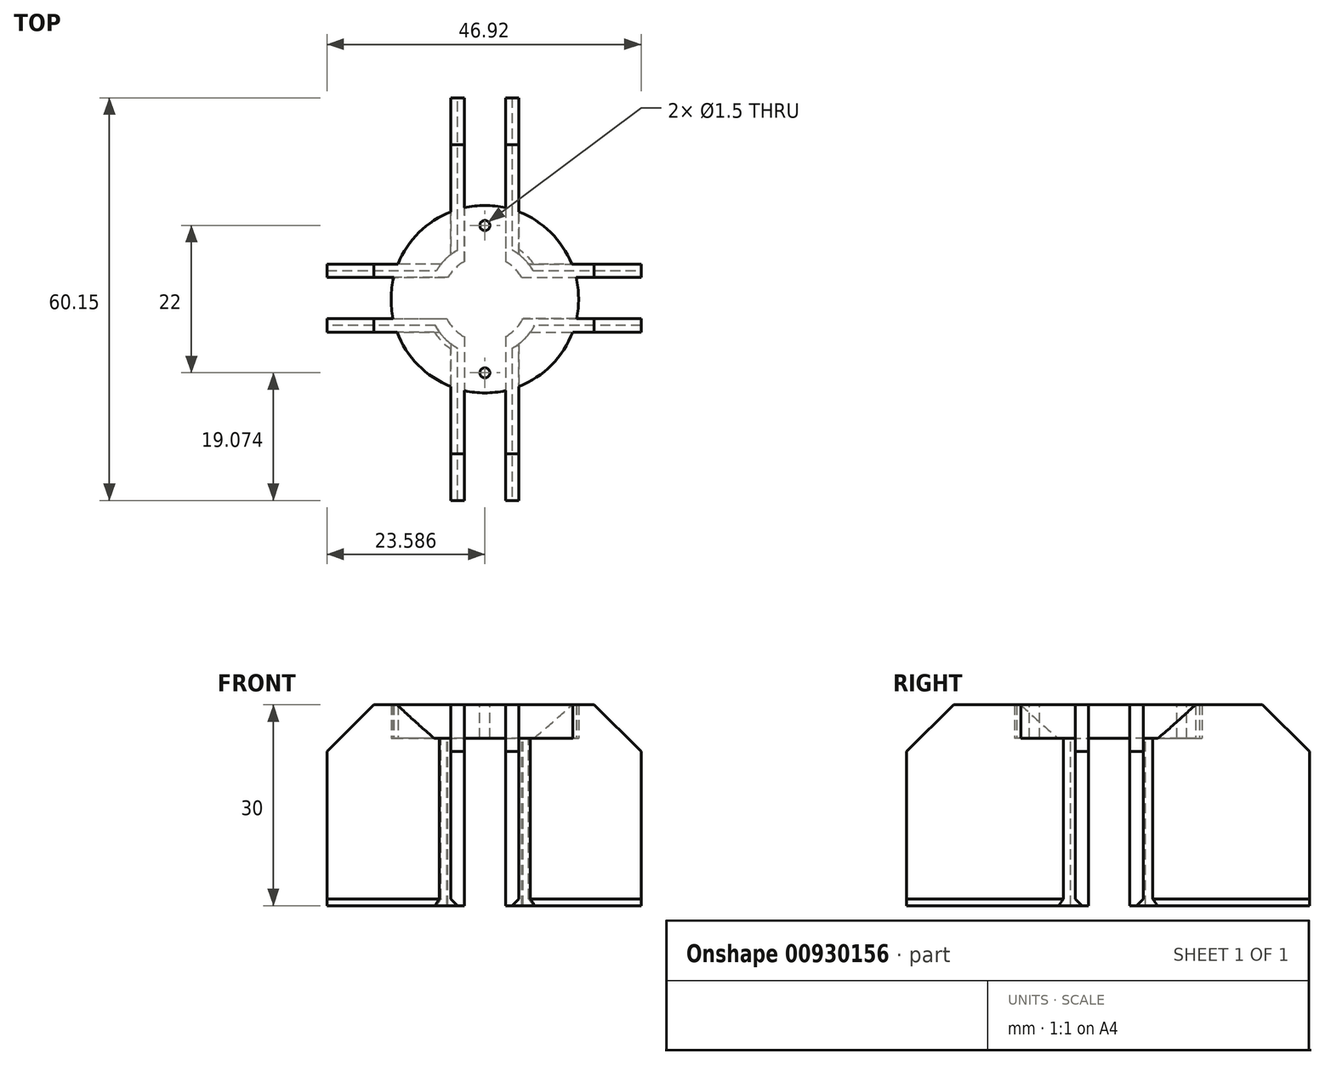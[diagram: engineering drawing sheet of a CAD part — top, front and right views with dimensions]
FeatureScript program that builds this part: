
annotation { "Feature Type Name" : "Feature", "Feature Type Description" : "" }
export const myFeature = defineFeature(function(context is Context, id is Id, definition is map)
    precondition{}
    {
        {
            var Q0;
            Q0=qCreatedBy(makeId("Top.planeOp"),FACE);
            var sketch = newSketch(context, id + "F0", { "sketchPlane" : qUnion([Q0])});
            skLineSegment(sketch, "E0.bottom", {"start": v(-2.63, 27.34) * mm, "end": v(3.52, 27.34) * mm});
            skLineSegment(sketch, "E0.top", {"start": v(-2.63, -28.81) * mm, "end": v(3.52, -28.81) * mm});
            skLineSegment(sketch, "E0.left", {"start": v(-2.63, 27.34) * mm, "end": v(-2.63, 4.86) * mm});
            skLineSegment(sketch, "E0.right", {"start": v(3.52, 27.34) * mm, "end": v(3.52, 4.86) * mm});
            skLineSegment(sketch, "E1.bottom", {"start": v(-21.14, 2.5) * mm, "end": v(-5.06, 2.5) * mm});
            skLineSegment(sketch, "E1.top", {"start": v(-21.14, -3.64) * mm, "end": v(-5.24, -3.64) * mm});
            skLineSegment(sketch, "E1.left", {"start": v(-21.14, 2.5) * mm, "end": v(-21.14, -3.64) * mm});
            skLineSegment(sketch, "E1.right", {"start": v(21.78, 2.5) * mm, "end": v(21.78, -3.64) * mm});
            skLineSegment(sketch, "E2.trimOffspring", {"start": v(-2.63, -6.34) * mm, "end": v(-2.63, -28.81) * mm});
            skLineSegment(sketch, "E3.trimOffspring", {"start": v(3.52, -6.34) * mm, "end": v(3.52, -28.81) * mm});
            skLineSegment(sketch, "E4.trimOffspring", {"start": v(5.95, 2.5) * mm, "end": v(21.78, 2.5) * mm});
            skLineSegment(sketch, "E5.trimOffspring", {"start": v(6.14, -3.64) * mm, "end": v(21.78, -3.64) * mm});
            skArc(sketch, "E6", {"start": v(-2.63, 4.86) * mm, "mid": v(-4, 3.85) * mm, "end": v(-5.06, 2.5) * mm});
            skArc(sketch, "E7.trimOffspring", {"start": v(5.95, 2.5) * mm, "mid": v(4.9, 3.85) * mm, "end": v(3.52, 4.86) * mm});
            skArc(sketch, "E8.trimOffspring", {"start": v(3.52, -6.34) * mm, "mid": v(5.03, -5.19) * mm, "end": v(6.14, -3.64) * mm});
            skArc(sketch, "E9.trimOffspring", {"start": v(-5.24, -3.64) * mm, "mid": v(-4.14, -5.19) * mm, "end": v(-2.63, -6.34) * mm});
            skLineSegment(sketch, "E10.0", {"start": v(-4.63, 29.34) * mm, "end": v(5.52, 29.34) * mm});
            skLineSegment(sketch, "E10.1", {"start": v(5.52, 29.34) * mm, "end": v(5.52, 5.94) * mm});
            skArc(sketch, "E10.2", {"start": v(7, 4.5) * mm, "mid": v(6.3, 5.27) * mm, "end": v(5.52, 5.94) * mm});
            skLineSegment(sketch, "E10.3", {"start": v(7, 4.5) * mm, "end": v(23.78, 4.5) * mm});
            skLineSegment(sketch, "E10.4", {"start": v(23.78, 4.5) * mm, "end": v(23.78, -5.64) * mm});
            skLineSegment(sketch, "E10.5", {"start": v(-23.14, -5.64) * mm, "end": v(-6.36, -5.64) * mm});
            skLineSegment(sketch, "E10.6", {"start": v(-23.14, 4.5) * mm, "end": v(-23.14, -5.64) * mm});
            skLineSegment(sketch, "E10.7", {"start": v(-23.14, 4.5) * mm, "end": v(-6.1, 4.5) * mm});
            skArc(sketch, "E10.8", {"start": v(-4.63, 5.94) * mm, "mid": v(-5.4, 5.27) * mm, "end": v(-6.1, 4.5) * mm});
            skArc(sketch, "E10.9", {"start": v(-6.36, -5.64) * mm, "mid": v(-5.56, -6.6) * mm, "end": v(-4.63, -7.42) * mm});
            skLineSegment(sketch, "E10.10", {"start": v(-4.63, -7.42) * mm, "end": v(-4.63, -30.81) * mm});
            skLineSegment(sketch, "E10.11", {"start": v(-4.63, -30.81) * mm, "end": v(5.52, -30.81) * mm});
            skLineSegment(sketch, "E10.12", {"start": v(5.52, -7.42) * mm, "end": v(5.52, -30.81) * mm});
            skArc(sketch, "E10.13", {"start": v(5.52, -7.42) * mm, "mid": v(6.45, -6.6) * mm, "end": v(7.25, -5.64) * mm});
            skLineSegment(sketch, "E10.14", {"start": v(-4.63, 29.34) * mm, "end": v(-4.63, 5.94) * mm});
            skLineSegment(sketch, "E10.15", {"start": v(7.25, -5.64) * mm, "end": v(23.78, -5.64) * mm});
            skSolve(sketch);
        }
        {
            var Q0;
            Q0=makeQuery(id+"F0.imprint","IMPRINT",FACE,{"disambiguationData":[TD([[makeQuery(id+"F0.imprint","IMPRINT",EDGE,{"derivedFrom":sQuery(id+"F0.wireOp",EDGE,"E0.bottom")}),1.0]])]});
            extrude(context, id + "F1", {"entities" : qUnion([Q0]), "oppositeDirection" : true, "depth" : 25 * mm, "offsetDistance" : 25 * mm});
        }
        {
            var Q0;
            Q0=makeQuery(id+"F1.opExtrude","CAP_FACE",FACE,{"disambiguationData":[OSD([sQuery(id+"F0.wireOp",EDGE,"E0.bottom"),sQuery(id+"F0.wireOp",EDGE,"E0.top"),sQuery(id+"F0.wireOp",EDGE,"E0.left"),sQuery(id+"F0.wireOp",EDGE,"E0.right"),sQuery(id+"F0.wireOp",EDGE,"E1.bottom"),sQuery(id+"F0.wireOp",EDGE,"E1.top"),sQuery(id+"F0.wireOp",EDGE,"E1.left"),sQuery(id+"F0.wireOp",EDGE,"E1.right"),sQuery(id+"F0.wireOp",EDGE,"E2.trimOffspring"),sQuery(id+"F0.wireOp",EDGE,"E3.trimOffspring"),sQuery(id+"F0.wireOp",EDGE,"E4.trimOffspring"),sQuery(id+"F0.wireOp",EDGE,"E5.trimOffspring"),sQuery(id+"F0.wireOp",EDGE,"E6"),sQuery(id+"F0.wireOp",EDGE,"E7.trimOffspring"),sQuery(id+"F0.wireOp",EDGE,"E8.trimOffspring"),sQuery(id+"F0.wireOp",EDGE,"E9.trimOffspring"),sQuery(id+"F0.wireOp",EDGE,"E10.0"),sQuery(id+"F0.wireOp",EDGE,"E10.1"),sQuery(id+"F0.wireOp",EDGE,"E10.2"),sQuery(id+"F0.wireOp",EDGE,"E10.3"),sQuery(id+"F0.wireOp",EDGE,"E10.4"),sQuery(id+"F0.wireOp",EDGE,"E10.5"),sQuery(id+"F0.wireOp",EDGE,"E10.6"),sQuery(id+"F0.wireOp",EDGE,"E10.7"),sQuery(id+"F0.wireOp",EDGE,"E10.8"),sQuery(id+"F0.wireOp",EDGE,"E10.9"),sQuery(id+"F0.wireOp",EDGE,"E10.10"),sQuery(id+"F0.wireOp",EDGE,"E10.11"),sQuery(id+"F0.wireOp",EDGE,"E10.12"),sQuery(id+"F0.wireOp",EDGE,"E10.13"),sQuery(id+"F0.wireOp",EDGE,"E10.14"),sQuery(id+"F0.wireOp",EDGE,"E10.15")])],"isStart":true});
            var sketch = newSketch(context, id + "F2", { "sketchPlane" : qUnion([Q0])});
            skLineSegment(sketch, "E11", {"start": v(-2.63, 27.34) * mm, "end": v(-2.63, 29.34) * mm});
            skLineSegment(sketch, "E12", {"start": v(-2.63, 29.34) * mm, "end": v(3.52, 29.34) * mm});
            skLineSegment(sketch, "E13", {"start": v(3.52, 29.34) * mm, "end": v(3.52, 27.34) * mm});
            skLineSegment(sketch, "E14", {"start": v(3.52, 27.34) * mm, "end": v(-2.63, 27.34) * mm});
            skLineSegment(sketch, "E15", {"start": v(-21.14, 2.5) * mm, "end": v(-23.14, 2.5) * mm});
            skLineSegment(sketch, "E16", {"start": v(-23.14, 2.5) * mm, "end": v(-23.14, -3.64) * mm});
            skLineSegment(sketch, "E17", {"start": v(-23.14, -3.64) * mm, "end": v(-21.14, -3.64) * mm});
            skLineSegment(sketch, "E18", {"start": v(-21.14, -3.64) * mm, "end": v(-21.14, 2.5) * mm});
            skLineSegment(sketch, "E19", {"start": v(21.78, 2.5) * mm, "end": v(23.78, 2.5) * mm});
            skLineSegment(sketch, "E20", {"start": v(23.78, 2.5) * mm, "end": v(23.78, -3.64) * mm});
            skLineSegment(sketch, "E21", {"start": v(23.78, -3.64) * mm, "end": v(21.78, -3.64) * mm});
            skLineSegment(sketch, "E22", {"start": v(21.78, -3.64) * mm, "end": v(21.78, 2.5) * mm});
            skLineSegment(sketch, "E23", {"start": v(-2.63, -28.81) * mm, "end": v(-2.63, -30.81) * mm});
            skLineSegment(sketch, "E24", {"start": v(-2.63, -30.81) * mm, "end": v(3.52, -30.81) * mm});
            skLineSegment(sketch, "E25", {"start": v(3.52, -30.81) * mm, "end": v(3.52, -28.81) * mm});
            skLineSegment(sketch, "E26", {"start": v(3.52, -28.81) * mm, "end": v(-2.63, -28.81) * mm});
            skSolve(sketch);
        }
        {
            var Q0;
            Q0=makeQuery(id+"F2.imprint","IMPRINT",FACE,{"disambiguationData":[TD([[makeQuery(id+"F2.imprint","IMPRINT",EDGE,{"derivedFrom":sQuery(id+"F2.wireOp",EDGE,"E11")}),-1.0]])]});
            var Q1;
            Q1=makeQuery(id+"F2.imprint","IMPRINT",FACE,{"disambiguationData":[TD([[makeQuery(id+"F2.imprint","IMPRINT",EDGE,{"derivedFrom":sQuery(id+"F2.wireOp",EDGE,"E15")}),1.0]])]});
            var Q2;
            Q2=makeQuery(id+"F2.imprint","IMPRINT",FACE,{"disambiguationData":[TD([[makeQuery(id+"F2.imprint","IMPRINT",EDGE,{"derivedFrom":sQuery(id+"F2.wireOp",EDGE,"E19")}),-1.0]])]});
            var Q3;
            Q3=makeQuery(id+"F2.imprint","IMPRINT",FACE,{"disambiguationData":[TD([[makeQuery(id+"F2.imprint","IMPRINT",EDGE,{"derivedFrom":sQuery(id+"F2.wireOp",EDGE,"E23")}),1.0]])]});
            extrude(context, id + "F3", {"entities" : qUnion([Q0, Q1, Q2, Q3]), "operationType" : NewBodyOperationType.REMOVE, "endBound" : BoundingType.UP_TO_NEXT, "oppositeDirection" : true, "depth" : 25 * mm, "offsetDistance" : 25 * mm});
        }
        {
            var Q0;
            Q0=qCreatedBy(makeId("Top.planeOp"),FACE);
            var sketch = newSketch(context, id + "F4", { "sketchPlane" : qUnion([Q0])});
            skLineSegment(sketch, "E27.0.0", {"start": v(5.52, 29.34) * mm, "end": v(3.52, 29.34) * mm});
            skLineSegment(sketch, "E27.0.1", {"start": v(3.52, 29.34) * mm, "end": v(3.52, 4.86) * mm});
            skArc(sketch, "E27.0.2", {"start": v(3.52, 4.86) * mm, "mid": v(4.9, 3.85) * mm, "end": v(5.95, 2.5) * mm});
            skLineSegment(sketch, "E27.0.3", {"start": v(5.95, 2.5) * mm, "end": v(23.78, 2.5) * mm});
            skLineSegment(sketch, "E27.0.4", {"start": v(23.78, 2.5) * mm, "end": v(23.78, 4.5) * mm});
            skLineSegment(sketch, "E27.0.5", {"start": v(23.78, 4.5) * mm, "end": v(7, 4.5) * mm});
            skArc(sketch, "E27.0.6", {"start": v(7, 4.5) * mm, "mid": v(6.3, 5.27) * mm, "end": v(5.52, 5.94) * mm});
            skLineSegment(sketch, "E27.0.7", {"start": v(5.52, 5.94) * mm, "end": v(5.52, 29.34) * mm});
            skArc(sketch, "E28.0.0", {"start": v(-5.06, 2.5) * mm, "mid": v(-4, 3.85) * mm, "end": v(-2.63, 4.86) * mm});
            skLineSegment(sketch, "E28.0.1", {"start": v(-2.63, 4.86) * mm, "end": v(-2.63, 29.34) * mm});
            skLineSegment(sketch, "E28.0.2", {"start": v(-2.63, 29.34) * mm, "end": v(-4.63, 29.34) * mm});
            skLineSegment(sketch, "E28.0.3", {"start": v(-4.63, 29.34) * mm, "end": v(-4.63, 5.94) * mm});
            skArc(sketch, "E28.0.4", {"start": v(-4.63, 5.94) * mm, "mid": v(-5.4, 5.27) * mm, "end": v(-6.1, 4.5) * mm});
            skLineSegment(sketch, "E28.0.5", {"start": v(-6.1, 4.5) * mm, "end": v(-23.14, 4.5) * mm});
            skLineSegment(sketch, "E28.0.6", {"start": v(-23.14, 4.5) * mm, "end": v(-23.14, 2.5) * mm});
            skLineSegment(sketch, "E28.0.7", {"start": v(-23.14, 2.5) * mm, "end": v(-5.06, 2.5) * mm});
            skLineSegment(sketch, "E29.0.0", {"start": v(-5.24, -3.64) * mm, "end": v(-23.14, -3.64) * mm});
            skLineSegment(sketch, "E29.0.1", {"start": v(-23.14, -3.64) * mm, "end": v(-23.14, -5.64) * mm});
            skLineSegment(sketch, "E29.0.2", {"start": v(-23.14, -5.64) * mm, "end": v(-6.36, -5.64) * mm});
            skArc(sketch, "E29.0.3", {"start": v(-6.36, -5.64) * mm, "mid": v(-5.56, -6.6) * mm, "end": v(-4.63, -7.42) * mm});
            skLineSegment(sketch, "E29.0.4", {"start": v(-4.63, -7.42) * mm, "end": v(-4.63, -30.81) * mm});
            skLineSegment(sketch, "E29.0.5", {"start": v(-4.63, -30.81) * mm, "end": v(-2.63, -30.81) * mm});
            skLineSegment(sketch, "E29.0.6", {"start": v(-2.63, -30.81) * mm, "end": v(-2.63, -6.34) * mm});
            skArc(sketch, "E29.0.7", {"start": v(-2.63, -6.34) * mm, "mid": v(-4.14, -5.19) * mm, "end": v(-5.24, -3.64) * mm});
            skLineSegment(sketch, "E30.0.0", {"start": v(23.78, -5.64) * mm, "end": v(23.78, -3.64) * mm});
            skLineSegment(sketch, "E30.0.1", {"start": v(23.78, -3.64) * mm, "end": v(6.14, -3.64) * mm});
            skArc(sketch, "E30.0.2", {"start": v(6.14, -3.64) * mm, "mid": v(5.03, -5.19) * mm, "end": v(3.52, -6.34) * mm});
            skLineSegment(sketch, "E30.0.3", {"start": v(3.52, -6.34) * mm, "end": v(3.52, -30.81) * mm});
            skLineSegment(sketch, "E30.0.4", {"start": v(3.52, -30.81) * mm, "end": v(5.52, -30.81) * mm});
            skLineSegment(sketch, "E30.0.5", {"start": v(5.52, -30.81) * mm, "end": v(5.52, -7.42) * mm});
            skArc(sketch, "E30.0.6", {"start": v(5.52, -7.42) * mm, "mid": v(6.45, -6.6) * mm, "end": v(7.25, -5.64) * mm});
            skLineSegment(sketch, "E30.0.7", {"start": v(7.25, -5.64) * mm, "end": v(23.78, -5.64) * mm});
            skCircle(sketch, "E31", {"center": v(0.45, -0.74) * mm, "radius": 14 * mm});
            skSolve(sketch);
        }
        {
            var Q0;
            {var subQ14=sQuery(id+"F4.wireOp",EDGE,"E27.0.2");Q0=makeQuery(id+"F4.imprint","IMPRINT",FACE,{"disambiguationData":[TD([[makeQuery(id+"F4.imprint","IMPRINT",EDGE,{"derivedFrom":subQ14}),-1.0]])]});}
            var Q1;
            {var subQ1=sQuery(id+"F4.wireOp",EDGE,"E30.0.2");Q1=makeQuery(id+"F4.imprint","IMPRINT",FACE,{"disambiguationData":[TD([[makeQuery(id+"F4.imprint","IMPRINT",EDGE,{"derivedFrom":subQ1}),1.0]])]});}
            var Q2;
            {var subQ0=sQuery(id+"F4.wireOp",EDGE,"E28.0.4");Q2=makeQuery(id+"F4.imprint","IMPRINT",FACE,{"disambiguationData":[TD([[makeQuery(id+"F4.imprint","IMPRINT",EDGE,{"derivedFrom":subQ0}),-1.0]])]});}
            var Q3;
            {var subQ2=sQuery(id+"F4.wireOp",EDGE,"E28.0.0");Q3=makeQuery(id+"F4.imprint","IMPRINT",FACE,{"disambiguationData":[TD([[makeQuery(id+"F4.imprint","IMPRINT",EDGE,{"derivedFrom":subQ2}),1.0]])]});}
            var Q4;
            {var subQ0=sQuery(id+"F4.wireOp",EDGE,"E27.0.6");Q4=makeQuery(id+"F4.imprint","IMPRINT",FACE,{"disambiguationData":[TD([[makeQuery(id+"F4.imprint","IMPRINT",EDGE,{"derivedFrom":subQ0}),-1.0]])]});}
            var Q5;
            {var subQ1=sQuery(id+"F4.wireOp",EDGE,"E27.0.2");Q5=makeQuery(id+"F4.imprint","IMPRINT",FACE,{"disambiguationData":[TD([[makeQuery(id+"F4.imprint","IMPRINT",EDGE,{"derivedFrom":subQ1}),1.0]])]});}
            var Q6;
            {var subQ0=sQuery(id+"F4.wireOp",EDGE,"E30.0.6");Q6=makeQuery(id+"F4.imprint","IMPRINT",FACE,{"disambiguationData":[TD([[makeQuery(id+"F4.imprint","IMPRINT",EDGE,{"derivedFrom":subQ0}),-1.0]])]});}
            var Q7;
            {var subQ0=sQuery(id+"F4.wireOp",EDGE,"E29.0.3");Q7=makeQuery(id+"F4.imprint","IMPRINT",FACE,{"disambiguationData":[TD([[makeQuery(id+"F4.imprint","IMPRINT",EDGE,{"derivedFrom":subQ0}),-1.0]])]});}
            var Q8;
            {var subQ1=sQuery(id+"F4.wireOp",EDGE,"E29.0.3");Q8=makeQuery(id+"F4.imprint","IMPRINT",FACE,{"disambiguationData":[TD([[makeQuery(id+"F4.imprint","IMPRINT",EDGE,{"derivedFrom":subQ1}),1.0]])]});}
            extrude(context, id + "F5", {"entities" : qUnion([Q0, Q1, Q2, Q3, Q4, Q5, Q6, Q7, Q8]), "operationType" : NewBodyOperationType.ADD, "depth" : 5 * mm, "offsetDistance" : 25 * mm});
        }
        {
            var Q0;
            Q0=makeQuery(id+"F5.opExtrude","CAP_FACE",FACE,{"disambiguationData":[OSD([sQuery(id+"F4.wireOp",EDGE,"E31")])],"isStart":false});
            var sketch = newSketch(context, id + "F6", { "sketchPlane" : qUnion([Q0])});
            skCircle(sketch, "E32", {"center": v(0.45, 10.26) * mm, "radius": 0.75 * mm});
            skCircle(sketch, "E33", {"center": v(0.45, -11.74) * mm, "radius": 0.75 * mm});
            skLineSegment(sketch, "E34", {"start": v(0.45, 10.26) * mm, "end": v(0.45, -11.74) * mm, "construction": true});
            skLineSegment(sketch, "E35", {"start": v(0.45, 10.26) * mm, "end": v(0.45, 13.26) * mm, "construction": true});
            skPoint(sketch, "E36.startSnap0", {"position": v(0.45, -0.74) * mm});
            skLineSegment(sketch, "E37.0", {"start": v(-2.63, 12.92) * mm, "end": v(-2.63, 29.34) * mm, "construction": true});
            skLineSegment(sketch, "E38.0", {"start": v(3.52, 29.34) * mm, "end": v(3.52, 12.92) * mm, "construction": true});
            skLineSegment(sketch, "E39", {"start": v(-2.63, 21.13) * mm, "end": v(0.45, 13.26) * mm, "construction": true});
            skLineSegment(sketch, "E40", {"start": v(3.52, 21.13) * mm, "end": v(0.45, 13.26) * mm, "construction": true});
            skLineSegment(sketch, "E41.0", {"start": v(3.52, -14.4) * mm, "end": v(3.52, -30.81) * mm, "construction": true});
            skLineSegment(sketch, "E42.0", {"start": v(-2.63, -14.4) * mm, "end": v(-2.63, -30.81) * mm, "construction": true});
            skLineSegment(sketch, "E43", {"start": v(-2.63, -22.6) * mm, "end": v(0.45, -14.74) * mm, "construction": true});
            skLineSegment(sketch, "E44", {"start": v(3.52, -22.6) * mm, "end": v(0.45, -14.74) * mm, "construction": true});
            skLineSegment(sketch, "E45", {"start": v(0.45, -11.74) * mm, "end": v(0.45, -14.74) * mm, "construction": true});
            skSolve(sketch);
        }
        {
            var Q0;
            Q0=makeQuery(id+"F6.imprint","IMPRINT",FACE,{"disambiguationData":[TD([[makeQuery(id+"F6.imprint","IMPRINT",EDGE,{"derivedFrom":sQuery(id+"F6.wireOp",EDGE,"E32")}),1.0]])]});
            var Q1;
            Q1=makeQuery(id+"F6.imprint","IMPRINT",FACE,{"disambiguationData":[TD([[makeQuery(id+"F6.imprint","IMPRINT",EDGE,{"derivedFrom":sQuery(id+"F6.wireOp",EDGE,"E33")}),1.0]])]});
            extrude(context, id + "F7", {"entities" : qUnion([Q0, Q1]), "operationType" : NewBodyOperationType.REMOVE, "endBound" : BoundingType.UP_TO_NEXT, "oppositeDirection" : true, "depth" : 25 * mm, "offsetDistance" : 25 * mm});
        }
        {
            var Q0;
            {var subQ1=sQuery(id+"F0.wireOp",EDGE,"E10.14");var subQ3=sQuery(id+"F0.wireOp",EDGE,"E10.0");var subQ5=sQuery(id+"F0.wireOp",EDGE,"E0.left");var subQ6=makeQuery(id+"F1.opExtrude","SWEPT_FACE",FACE,{"disambiguationData":[OSD([subQ5])]});var subQ7=sQuery(id+"F0.wireOp",EDGE,"E1.bottom");var subQ8=sQuery(id+"F0.wireOp",EDGE,"E6");var subQ9=sQuery(id+"F0.wireOp",EDGE,"E10.7");var subQ10=sQuery(id+"F0.wireOp",EDGE,"E10.8");var subQ11=sQuery(id+"F0.wireOp",EDGE,"E10.6");Q0=makeQuery(id+"F5.boolean.opBoolean","SPLIT",FACE,{"disambiguationData":[TD([subQ6])],"derivedFrom":makeQuery(id+"F3.boolean.opBoolean","SPLIT",FACE,{"disambiguationData":[TD([subQ6])],"derivedFrom":makeQuery(id+"F1.opExtrude","CAP_FACE",FACE,{"disambiguationData":[OSD([sQuery(id+"F0.wireOp",EDGE,"E0.bottom"),sQuery(id+"F0.wireOp",EDGE,"E0.top"),subQ5,sQuery(id+"F0.wireOp",EDGE,"E0.right"),subQ7,sQuery(id+"F0.wireOp",EDGE,"E1.top"),sQuery(id+"F0.wireOp",EDGE,"E1.left"),sQuery(id+"F0.wireOp",EDGE,"E1.right"),sQuery(id+"F0.wireOp",EDGE,"E2.trimOffspring"),sQuery(id+"F0.wireOp",EDGE,"E3.trimOffspring"),sQuery(id+"F0.wireOp",EDGE,"E4.trimOffspring"),sQuery(id+"F0.wireOp",EDGE,"E5.trimOffspring"),subQ8,sQuery(id+"F0.wireOp",EDGE,"E7.trimOffspring"),sQuery(id+"F0.wireOp",EDGE,"E8.trimOffspring"),sQuery(id+"F0.wireOp",EDGE,"E9.trimOffspring"),subQ3,sQuery(id+"F0.wireOp",EDGE,"E10.1"),sQuery(id+"F0.wireOp",EDGE,"E10.2"),sQuery(id+"F0.wireOp",EDGE,"E10.3"),sQuery(id+"F0.wireOp",EDGE,"E10.4"),sQuery(id+"F0.wireOp",EDGE,"E10.5"),subQ11,subQ9,subQ10,sQuery(id+"F0.wireOp",EDGE,"E10.9"),sQuery(id+"F0.wireOp",EDGE,"E10.10"),sQuery(id+"F0.wireOp",EDGE,"E10.11"),sQuery(id+"F0.wireOp",EDGE,"E10.12"),sQuery(id+"F0.wireOp",EDGE,"E10.13"),subQ1,sQuery(id+"F0.wireOp",EDGE,"E10.15")])],"isStart":true})})});}
            var Q1;
            {var subQ1=sQuery(id+"F0.wireOp",EDGE,"E10.1");var subQ3=sQuery(id+"F0.wireOp",EDGE,"E10.0");var subQ5=sQuery(id+"F0.wireOp",EDGE,"E0.right");var subQ6=makeQuery(id+"F1.opExtrude","SWEPT_FACE",FACE,{"disambiguationData":[OSD([subQ5])]});var subQ7=sQuery(id+"F0.wireOp",EDGE,"E4.trimOffspring");var subQ8=sQuery(id+"F0.wireOp",EDGE,"E7.trimOffspring");var subQ9=sQuery(id+"F0.wireOp",EDGE,"E10.2");var subQ10=sQuery(id+"F0.wireOp",EDGE,"E10.3");var subQ11=sQuery(id+"F0.wireOp",EDGE,"E10.4");Q1=makeQuery(id+"F5.boolean.opBoolean","SPLIT",FACE,{"disambiguationData":[TD([subQ6])],"derivedFrom":makeQuery(id+"F3.boolean.opBoolean","SPLIT",FACE,{"disambiguationData":[TD([subQ6])],"derivedFrom":makeQuery(id+"F1.opExtrude","CAP_FACE",FACE,{"disambiguationData":[OSD([sQuery(id+"F0.wireOp",EDGE,"E0.bottom"),sQuery(id+"F0.wireOp",EDGE,"E0.top"),sQuery(id+"F0.wireOp",EDGE,"E0.left"),subQ5,sQuery(id+"F0.wireOp",EDGE,"E1.bottom"),sQuery(id+"F0.wireOp",EDGE,"E1.top"),sQuery(id+"F0.wireOp",EDGE,"E1.left"),sQuery(id+"F0.wireOp",EDGE,"E1.right"),sQuery(id+"F0.wireOp",EDGE,"E2.trimOffspring"),sQuery(id+"F0.wireOp",EDGE,"E3.trimOffspring"),subQ7,sQuery(id+"F0.wireOp",EDGE,"E5.trimOffspring"),sQuery(id+"F0.wireOp",EDGE,"E6"),subQ8,sQuery(id+"F0.wireOp",EDGE,"E8.trimOffspring"),sQuery(id+"F0.wireOp",EDGE,"E9.trimOffspring"),subQ3,subQ1,subQ9,subQ10,subQ11,sQuery(id+"F0.wireOp",EDGE,"E10.5"),sQuery(id+"F0.wireOp",EDGE,"E10.6"),sQuery(id+"F0.wireOp",EDGE,"E10.7"),sQuery(id+"F0.wireOp",EDGE,"E10.8"),sQuery(id+"F0.wireOp",EDGE,"E10.9"),sQuery(id+"F0.wireOp",EDGE,"E10.10"),sQuery(id+"F0.wireOp",EDGE,"E10.11"),sQuery(id+"F0.wireOp",EDGE,"E10.12"),sQuery(id+"F0.wireOp",EDGE,"E10.13"),sQuery(id+"F0.wireOp",EDGE,"E10.14"),sQuery(id+"F0.wireOp",EDGE,"E10.15")])],"isStart":true})})});}
            var Q2;
            {var subQ0=sQuery(id+"F0.wireOp",EDGE,"E10.3");var subQ3=sQuery(id+"F0.wireOp",EDGE,"E10.4");var subQ5=sQuery(id+"F0.wireOp",EDGE,"E4.trimOffspring");var subQ6=makeQuery(id+"F1.opExtrude","SWEPT_FACE",FACE,{"disambiguationData":[OSD([subQ5])]});var subQ7=sQuery(id+"F0.wireOp",EDGE,"E10.0");var subQ8=sQuery(id+"F0.wireOp",EDGE,"E7.trimOffspring");var subQ9=sQuery(id+"F0.wireOp",EDGE,"E0.right");var subQ10=sQuery(id+"F0.wireOp",EDGE,"E10.1");var subQ11=sQuery(id+"F0.wireOp",EDGE,"E10.2");Q2=makeQuery(id+"F5.boolean.opBoolean","SPLIT",FACE,{"disambiguationData":[TD([subQ6])],"derivedFrom":makeQuery(id+"F3.boolean.opBoolean","SPLIT",FACE,{"disambiguationData":[TD([makeQuery(id+"F1.opExtrude","SWEPT_FACE",FACE,{"disambiguationData":[OSD([subQ9])]})])],"derivedFrom":makeQuery(id+"F1.opExtrude","CAP_FACE",FACE,{"disambiguationData":[OSD([sQuery(id+"F0.wireOp",EDGE,"E0.bottom"),sQuery(id+"F0.wireOp",EDGE,"E0.top"),sQuery(id+"F0.wireOp",EDGE,"E0.left"),subQ9,sQuery(id+"F0.wireOp",EDGE,"E1.bottom"),sQuery(id+"F0.wireOp",EDGE,"E1.top"),sQuery(id+"F0.wireOp",EDGE,"E1.left"),sQuery(id+"F0.wireOp",EDGE,"E1.right"),sQuery(id+"F0.wireOp",EDGE,"E2.trimOffspring"),sQuery(id+"F0.wireOp",EDGE,"E3.trimOffspring"),subQ5,sQuery(id+"F0.wireOp",EDGE,"E5.trimOffspring"),sQuery(id+"F0.wireOp",EDGE,"E6"),subQ8,sQuery(id+"F0.wireOp",EDGE,"E8.trimOffspring"),sQuery(id+"F0.wireOp",EDGE,"E9.trimOffspring"),subQ7,subQ10,subQ11,subQ0,subQ3,sQuery(id+"F0.wireOp",EDGE,"E10.5"),sQuery(id+"F0.wireOp",EDGE,"E10.6"),sQuery(id+"F0.wireOp",EDGE,"E10.7"),sQuery(id+"F0.wireOp",EDGE,"E10.8"),sQuery(id+"F0.wireOp",EDGE,"E10.9"),sQuery(id+"F0.wireOp",EDGE,"E10.10"),sQuery(id+"F0.wireOp",EDGE,"E10.11"),sQuery(id+"F0.wireOp",EDGE,"E10.12"),sQuery(id+"F0.wireOp",EDGE,"E10.13"),sQuery(id+"F0.wireOp",EDGE,"E10.14"),sQuery(id+"F0.wireOp",EDGE,"E10.15")])],"isStart":true})})});}
            var Q3;
            {var subQ1=sQuery(id+"F0.wireOp",EDGE,"E10.4");var subQ3=sQuery(id+"F0.wireOp",EDGE,"E10.15");var subQ5=sQuery(id+"F0.wireOp",EDGE,"E5.trimOffspring");var subQ6=makeQuery(id+"F1.opExtrude","SWEPT_FACE",FACE,{"disambiguationData":[OSD([subQ5])]});var subQ7=sQuery(id+"F0.wireOp",EDGE,"E3.trimOffspring");var subQ8=sQuery(id+"F0.wireOp",EDGE,"E8.trimOffspring");var subQ9=sQuery(id+"F0.wireOp",EDGE,"E10.11");var subQ10=sQuery(id+"F0.wireOp",EDGE,"E10.12");var subQ11=sQuery(id+"F0.wireOp",EDGE,"E10.13");Q3=makeQuery(id+"F5.boolean.opBoolean","SPLIT",FACE,{"disambiguationData":[TD([subQ6])],"derivedFrom":makeQuery(id+"F3.boolean.opBoolean","SPLIT",FACE,{"disambiguationData":[TD([makeQuery(id+"F1.opExtrude","SWEPT_FACE",FACE,{"disambiguationData":[OSD([subQ7])]})])],"derivedFrom":makeQuery(id+"F1.opExtrude","CAP_FACE",FACE,{"disambiguationData":[OSD([sQuery(id+"F0.wireOp",EDGE,"E0.bottom"),sQuery(id+"F0.wireOp",EDGE,"E0.top"),sQuery(id+"F0.wireOp",EDGE,"E0.left"),sQuery(id+"F0.wireOp",EDGE,"E0.right"),sQuery(id+"F0.wireOp",EDGE,"E1.bottom"),sQuery(id+"F0.wireOp",EDGE,"E1.top"),sQuery(id+"F0.wireOp",EDGE,"E1.left"),sQuery(id+"F0.wireOp",EDGE,"E1.right"),sQuery(id+"F0.wireOp",EDGE,"E2.trimOffspring"),subQ7,sQuery(id+"F0.wireOp",EDGE,"E4.trimOffspring"),subQ5,sQuery(id+"F0.wireOp",EDGE,"E6"),sQuery(id+"F0.wireOp",EDGE,"E7.trimOffspring"),subQ8,sQuery(id+"F0.wireOp",EDGE,"E9.trimOffspring"),sQuery(id+"F0.wireOp",EDGE,"E10.0"),sQuery(id+"F0.wireOp",EDGE,"E10.1"),sQuery(id+"F0.wireOp",EDGE,"E10.2"),sQuery(id+"F0.wireOp",EDGE,"E10.3"),subQ1,sQuery(id+"F0.wireOp",EDGE,"E10.5"),sQuery(id+"F0.wireOp",EDGE,"E10.6"),sQuery(id+"F0.wireOp",EDGE,"E10.7"),sQuery(id+"F0.wireOp",EDGE,"E10.8"),sQuery(id+"F0.wireOp",EDGE,"E10.9"),sQuery(id+"F0.wireOp",EDGE,"E10.10"),subQ9,subQ10,subQ11,sQuery(id+"F0.wireOp",EDGE,"E10.14"),subQ3])],"isStart":true})})});}
            var Q4;
            {var subQ1=sQuery(id+"F0.wireOp",EDGE,"E1.bottom");var subQ2=makeQuery(id+"F1.opExtrude","SWEPT_FACE",FACE,{"disambiguationData":[OSD([subQ1])]});var subQ3=sQuery(id+"F0.wireOp",EDGE,"E10.7");var subQ5=sQuery(id+"F0.wireOp",EDGE,"E10.6");var subQ7=sQuery(id+"F0.wireOp",EDGE,"E10.0");var subQ8=sQuery(id+"F0.wireOp",EDGE,"E6");var subQ9=sQuery(id+"F0.wireOp",EDGE,"E0.left");var subQ10=sQuery(id+"F0.wireOp",EDGE,"E10.8");var subQ11=sQuery(id+"F0.wireOp",EDGE,"E10.14");Q4=makeQuery(id+"F5.boolean.opBoolean","SPLIT",FACE,{"disambiguationData":[TD([subQ2])],"derivedFrom":makeQuery(id+"F3.boolean.opBoolean","SPLIT",FACE,{"disambiguationData":[TD([makeQuery(id+"F1.opExtrude","SWEPT_FACE",FACE,{"disambiguationData":[OSD([subQ9])]})])],"derivedFrom":makeQuery(id+"F1.opExtrude","CAP_FACE",FACE,{"disambiguationData":[OSD([sQuery(id+"F0.wireOp",EDGE,"E0.bottom"),sQuery(id+"F0.wireOp",EDGE,"E0.top"),subQ9,sQuery(id+"F0.wireOp",EDGE,"E0.right"),subQ1,sQuery(id+"F0.wireOp",EDGE,"E1.top"),sQuery(id+"F0.wireOp",EDGE,"E1.left"),sQuery(id+"F0.wireOp",EDGE,"E1.right"),sQuery(id+"F0.wireOp",EDGE,"E2.trimOffspring"),sQuery(id+"F0.wireOp",EDGE,"E3.trimOffspring"),sQuery(id+"F0.wireOp",EDGE,"E4.trimOffspring"),sQuery(id+"F0.wireOp",EDGE,"E5.trimOffspring"),subQ8,sQuery(id+"F0.wireOp",EDGE,"E7.trimOffspring"),sQuery(id+"F0.wireOp",EDGE,"E8.trimOffspring"),sQuery(id+"F0.wireOp",EDGE,"E9.trimOffspring"),subQ7,sQuery(id+"F0.wireOp",EDGE,"E10.1"),sQuery(id+"F0.wireOp",EDGE,"E10.2"),sQuery(id+"F0.wireOp",EDGE,"E10.3"),sQuery(id+"F0.wireOp",EDGE,"E10.4"),sQuery(id+"F0.wireOp",EDGE,"E10.5"),subQ5,subQ3,subQ10,sQuery(id+"F0.wireOp",EDGE,"E10.9"),sQuery(id+"F0.wireOp",EDGE,"E10.10"),sQuery(id+"F0.wireOp",EDGE,"E10.11"),sQuery(id+"F0.wireOp",EDGE,"E10.12"),sQuery(id+"F0.wireOp",EDGE,"E10.13"),subQ11,sQuery(id+"F0.wireOp",EDGE,"E10.15")])],"isStart":true})})});}
            var Q5;
            {var subQ0=sQuery(id+"F0.wireOp",EDGE,"E10.6");var subQ2=sQuery(id+"F0.wireOp",EDGE,"E10.5");var subQ5=sQuery(id+"F0.wireOp",EDGE,"E1.top");var subQ6=makeQuery(id+"F1.opExtrude","SWEPT_FACE",FACE,{"disambiguationData":[OSD([subQ5])]});var subQ7=sQuery(id+"F0.wireOp",EDGE,"E2.trimOffspring");var subQ8=sQuery(id+"F0.wireOp",EDGE,"E9.trimOffspring");var subQ9=sQuery(id+"F0.wireOp",EDGE,"E10.10");var subQ10=sQuery(id+"F0.wireOp",EDGE,"E10.11");var subQ11=sQuery(id+"F0.wireOp",EDGE,"E10.9");Q5=makeQuery(id+"F5.boolean.opBoolean","SPLIT",FACE,{"disambiguationData":[TD([subQ6])],"derivedFrom":makeQuery(id+"F3.boolean.opBoolean","SPLIT",FACE,{"disambiguationData":[TD([subQ6])],"derivedFrom":makeQuery(id+"F1.opExtrude","CAP_FACE",FACE,{"disambiguationData":[OSD([sQuery(id+"F0.wireOp",EDGE,"E0.bottom"),sQuery(id+"F0.wireOp",EDGE,"E0.top"),sQuery(id+"F0.wireOp",EDGE,"E0.left"),sQuery(id+"F0.wireOp",EDGE,"E0.right"),sQuery(id+"F0.wireOp",EDGE,"E1.bottom"),subQ5,sQuery(id+"F0.wireOp",EDGE,"E1.left"),sQuery(id+"F0.wireOp",EDGE,"E1.right"),subQ7,sQuery(id+"F0.wireOp",EDGE,"E3.trimOffspring"),sQuery(id+"F0.wireOp",EDGE,"E4.trimOffspring"),sQuery(id+"F0.wireOp",EDGE,"E5.trimOffspring"),sQuery(id+"F0.wireOp",EDGE,"E6"),sQuery(id+"F0.wireOp",EDGE,"E7.trimOffspring"),sQuery(id+"F0.wireOp",EDGE,"E8.trimOffspring"),subQ8,sQuery(id+"F0.wireOp",EDGE,"E10.0"),sQuery(id+"F0.wireOp",EDGE,"E10.1"),sQuery(id+"F0.wireOp",EDGE,"E10.2"),sQuery(id+"F0.wireOp",EDGE,"E10.3"),sQuery(id+"F0.wireOp",EDGE,"E10.4"),subQ2,subQ0,sQuery(id+"F0.wireOp",EDGE,"E10.7"),sQuery(id+"F0.wireOp",EDGE,"E10.8"),subQ11,subQ9,subQ10,sQuery(id+"F0.wireOp",EDGE,"E10.12"),sQuery(id+"F0.wireOp",EDGE,"E10.13"),sQuery(id+"F0.wireOp",EDGE,"E10.14"),sQuery(id+"F0.wireOp",EDGE,"E10.15")])],"isStart":true})})});}
            var Q6;
            {var subQ1=sQuery(id+"F0.wireOp",EDGE,"E10.10");var subQ3=sQuery(id+"F0.wireOp",EDGE,"E10.11");var subQ5=sQuery(id+"F0.wireOp",EDGE,"E2.trimOffspring");var subQ6=makeQuery(id+"F1.opExtrude","SWEPT_FACE",FACE,{"disambiguationData":[OSD([subQ5])]});var subQ7=sQuery(id+"F0.wireOp",EDGE,"E10.5");var subQ8=sQuery(id+"F0.wireOp",EDGE,"E9.trimOffspring");var subQ9=sQuery(id+"F0.wireOp",EDGE,"E1.top");var subQ10=sQuery(id+"F0.wireOp",EDGE,"E10.6");var subQ11=sQuery(id+"F0.wireOp",EDGE,"E10.9");Q6=makeQuery(id+"F5.boolean.opBoolean","SPLIT",FACE,{"disambiguationData":[TD([subQ6])],"derivedFrom":makeQuery(id+"F3.boolean.opBoolean","SPLIT",FACE,{"disambiguationData":[TD([makeQuery(id+"F1.opExtrude","SWEPT_FACE",FACE,{"disambiguationData":[OSD([subQ9])]})])],"derivedFrom":makeQuery(id+"F1.opExtrude","CAP_FACE",FACE,{"disambiguationData":[OSD([sQuery(id+"F0.wireOp",EDGE,"E0.bottom"),sQuery(id+"F0.wireOp",EDGE,"E0.top"),sQuery(id+"F0.wireOp",EDGE,"E0.left"),sQuery(id+"F0.wireOp",EDGE,"E0.right"),sQuery(id+"F0.wireOp",EDGE,"E1.bottom"),subQ9,sQuery(id+"F0.wireOp",EDGE,"E1.left"),sQuery(id+"F0.wireOp",EDGE,"E1.right"),subQ5,sQuery(id+"F0.wireOp",EDGE,"E3.trimOffspring"),sQuery(id+"F0.wireOp",EDGE,"E4.trimOffspring"),sQuery(id+"F0.wireOp",EDGE,"E5.trimOffspring"),sQuery(id+"F0.wireOp",EDGE,"E6"),sQuery(id+"F0.wireOp",EDGE,"E7.trimOffspring"),sQuery(id+"F0.wireOp",EDGE,"E8.trimOffspring"),subQ8,sQuery(id+"F0.wireOp",EDGE,"E10.0"),sQuery(id+"F0.wireOp",EDGE,"E10.1"),sQuery(id+"F0.wireOp",EDGE,"E10.2"),sQuery(id+"F0.wireOp",EDGE,"E10.3"),sQuery(id+"F0.wireOp",EDGE,"E10.4"),subQ7,subQ10,sQuery(id+"F0.wireOp",EDGE,"E10.7"),sQuery(id+"F0.wireOp",EDGE,"E10.8"),subQ11,subQ1,subQ3,sQuery(id+"F0.wireOp",EDGE,"E10.12"),sQuery(id+"F0.wireOp",EDGE,"E10.13"),sQuery(id+"F0.wireOp",EDGE,"E10.14"),sQuery(id+"F0.wireOp",EDGE,"E10.15")])],"isStart":true})})});}
            var Q7;
            {var subQ1=sQuery(id+"F0.wireOp",EDGE,"E10.12");var subQ3=sQuery(id+"F0.wireOp",EDGE,"E10.11");var subQ5=sQuery(id+"F0.wireOp",EDGE,"E3.trimOffspring");var subQ6=makeQuery(id+"F1.opExtrude","SWEPT_FACE",FACE,{"disambiguationData":[OSD([subQ5])]});var subQ7=sQuery(id+"F0.wireOp",EDGE,"E10.4");var subQ8=sQuery(id+"F0.wireOp",EDGE,"E10.15");var subQ9=sQuery(id+"F0.wireOp",EDGE,"E5.trimOffspring");var subQ10=sQuery(id+"F0.wireOp",EDGE,"E8.trimOffspring");var subQ11=sQuery(id+"F0.wireOp",EDGE,"E10.13");Q7=makeQuery(id+"F5.boolean.opBoolean","SPLIT",FACE,{"disambiguationData":[TD([subQ6])],"derivedFrom":makeQuery(id+"F3.boolean.opBoolean","SPLIT",FACE,{"disambiguationData":[TD([subQ6])],"derivedFrom":makeQuery(id+"F1.opExtrude","CAP_FACE",FACE,{"disambiguationData":[OSD([sQuery(id+"F0.wireOp",EDGE,"E0.bottom"),sQuery(id+"F0.wireOp",EDGE,"E0.top"),sQuery(id+"F0.wireOp",EDGE,"E0.left"),sQuery(id+"F0.wireOp",EDGE,"E0.right"),sQuery(id+"F0.wireOp",EDGE,"E1.bottom"),sQuery(id+"F0.wireOp",EDGE,"E1.top"),sQuery(id+"F0.wireOp",EDGE,"E1.left"),sQuery(id+"F0.wireOp",EDGE,"E1.right"),sQuery(id+"F0.wireOp",EDGE,"E2.trimOffspring"),subQ5,sQuery(id+"F0.wireOp",EDGE,"E4.trimOffspring"),subQ9,sQuery(id+"F0.wireOp",EDGE,"E6"),sQuery(id+"F0.wireOp",EDGE,"E7.trimOffspring"),subQ10,sQuery(id+"F0.wireOp",EDGE,"E9.trimOffspring"),sQuery(id+"F0.wireOp",EDGE,"E10.0"),sQuery(id+"F0.wireOp",EDGE,"E10.1"),sQuery(id+"F0.wireOp",EDGE,"E10.2"),sQuery(id+"F0.wireOp",EDGE,"E10.3"),subQ7,sQuery(id+"F0.wireOp",EDGE,"E10.5"),sQuery(id+"F0.wireOp",EDGE,"E10.6"),sQuery(id+"F0.wireOp",EDGE,"E10.7"),sQuery(id+"F0.wireOp",EDGE,"E10.8"),sQuery(id+"F0.wireOp",EDGE,"E10.9"),sQuery(id+"F0.wireOp",EDGE,"E10.10"),subQ3,subQ1,subQ11,sQuery(id+"F0.wireOp",EDGE,"E10.14"),subQ8])],"isStart":true})})});}
            extrude(context, id + "F8", {"entities" : qUnion([Q0, Q1, Q2, Q3, Q4, Q5, Q6, Q7]), "operationType" : NewBodyOperationType.ADD, "depth" : 5 * mm, "offsetDistance" : 25 * mm});
        }
        {
            var Q0;
            {var subQ1=sQuery(id+"F0.wireOp",EDGE,"E10.6");var subQ2=sQuery(id+"F0.wireOp",EDGE,"E1.bottom");Q0=makeQuery(id+"F8.opExtrude","CAP_EDGE",EDGE,{"disambiguationData":[OSD([subQ1]),TDD([makeQuery(id+"F3.boolean.opBoolean","SPLIT",EDGE,{"disambiguationData":[TD([makeQuery(id+"F1.opExtrude","SWEPT_FACE",FACE,{"disambiguationData":[OSD([subQ2])]})])],"derivedFrom":makeQuery(id+"F1.opExtrude","CAP_EDGE",EDGE,{"disambiguationData":[OSD([subQ1])],"isStart":true})})])],"isStart":false});}
            var Q1;
            {var subQ0=sQuery(id+"F0.wireOp",EDGE,"E10.6");var subQ2=sQuery(id+"F0.wireOp",EDGE,"E1.top");Q1=makeQuery(id+"F8.opExtrude","CAP_EDGE",EDGE,{"disambiguationData":[OSD([subQ0]),TDD([makeQuery(id+"F3.boolean.opBoolean","SPLIT",EDGE,{"disambiguationData":[TD([makeQuery(id+"F1.opExtrude","SWEPT_FACE",FACE,{"disambiguationData":[OSD([subQ2])]})])],"derivedFrom":makeQuery(id+"F1.opExtrude","CAP_EDGE",EDGE,{"disambiguationData":[OSD([subQ0])],"isStart":true})})])],"isStart":false});}
            var Q2;
            {var subQ0=sQuery(id+"F0.wireOp",EDGE,"E10.11");var subQ2=sQuery(id+"F0.wireOp",EDGE,"E2.trimOffspring");Q2=makeQuery(id+"F8.opExtrude","CAP_EDGE",EDGE,{"disambiguationData":[OSD([subQ0]),TDD([makeQuery(id+"F3.boolean.opBoolean","SPLIT",EDGE,{"disambiguationData":[TD([makeQuery(id+"F1.opExtrude","SWEPT_FACE",FACE,{"disambiguationData":[OSD([subQ2])]})])],"derivedFrom":makeQuery(id+"F1.opExtrude","CAP_EDGE",EDGE,{"disambiguationData":[OSD([subQ0])],"isStart":true})})])],"isStart":false});}
            var Q3;
            {var subQ1=sQuery(id+"F0.wireOp",EDGE,"E10.11");var subQ2=sQuery(id+"F0.wireOp",EDGE,"E3.trimOffspring");Q3=makeQuery(id+"F8.opExtrude","CAP_EDGE",EDGE,{"disambiguationData":[OSD([subQ1]),TDD([makeQuery(id+"F3.boolean.opBoolean","SPLIT",EDGE,{"disambiguationData":[TD([makeQuery(id+"F1.opExtrude","SWEPT_FACE",FACE,{"disambiguationData":[OSD([subQ2])]})])],"derivedFrom":makeQuery(id+"F1.opExtrude","CAP_EDGE",EDGE,{"disambiguationData":[OSD([subQ1])],"isStart":true})})])],"isStart":false});}
            var Q4;
            {var subQ0=sQuery(id+"F0.wireOp",EDGE,"E10.4");var subQ2=sQuery(id+"F0.wireOp",EDGE,"E5.trimOffspring");Q4=makeQuery(id+"F8.opExtrude","CAP_EDGE",EDGE,{"disambiguationData":[OSD([subQ0]),TDD([makeQuery(id+"F3.boolean.opBoolean","SPLIT",EDGE,{"disambiguationData":[TD([makeQuery(id+"F1.opExtrude","SWEPT_FACE",FACE,{"disambiguationData":[OSD([subQ2])]})])],"derivedFrom":makeQuery(id+"F1.opExtrude","CAP_EDGE",EDGE,{"disambiguationData":[OSD([subQ0])],"isStart":true})})])],"isStart":false});}
            var Q5;
            {var subQ0=sQuery(id+"F0.wireOp",EDGE,"E10.4");var subQ1=sQuery(id+"F0.wireOp",EDGE,"E4.trimOffspring");Q5=makeQuery(id+"F8.opExtrude","CAP_EDGE",EDGE,{"disambiguationData":[OSD([subQ0]),TDD([makeQuery(id+"F3.boolean.opBoolean","SPLIT",EDGE,{"disambiguationData":[TD([makeQuery(id+"F1.opExtrude","SWEPT_FACE",FACE,{"disambiguationData":[OSD([subQ1])]})])],"derivedFrom":makeQuery(id+"F1.opExtrude","CAP_EDGE",EDGE,{"disambiguationData":[OSD([subQ0])],"isStart":true})})])],"isStart":false});}
            var Q6;
            {var subQ1=sQuery(id+"F0.wireOp",EDGE,"E10.0");var subQ2=sQuery(id+"F0.wireOp",EDGE,"E0.left");Q6=makeQuery(id+"F8.opExtrude","CAP_EDGE",EDGE,{"disambiguationData":[OSD([subQ1]),TDD([makeQuery(id+"F3.boolean.opBoolean","SPLIT",EDGE,{"disambiguationData":[TD([makeQuery(id+"F1.opExtrude","SWEPT_FACE",FACE,{"disambiguationData":[OSD([subQ2])]})])],"derivedFrom":makeQuery(id+"F1.opExtrude","CAP_EDGE",EDGE,{"disambiguationData":[OSD([subQ1])],"isStart":true})})])],"isStart":false});}
            var Q7;
            {var subQ1=sQuery(id+"F0.wireOp",EDGE,"E10.0");var subQ2=sQuery(id+"F0.wireOp",EDGE,"E0.right");Q7=makeQuery(id+"F8.opExtrude","CAP_EDGE",EDGE,{"disambiguationData":[OSD([subQ1]),TDD([makeQuery(id+"F3.boolean.opBoolean","SPLIT",EDGE,{"disambiguationData":[TD([makeQuery(id+"F1.opExtrude","SWEPT_FACE",FACE,{"disambiguationData":[OSD([subQ2])]})])],"derivedFrom":makeQuery(id+"F1.opExtrude","CAP_EDGE",EDGE,{"disambiguationData":[OSD([subQ1])],"isStart":true})})])],"isStart":false});}
            chamfer(context, id + "F9", {"entities" : qUnion([Q0, Q1, Q2, Q3, Q4, Q5, Q6, Q7]), "width" : 7 * mm, "tangentPropagation" : true});
        }
        {
            var Q0;
            {var subQ0=sQuery(id+"F4.wireOp",EDGE,"E31");var subQ1=makeQuery(id+"F5.opExtrude","SWEPT_FACE",FACE,{"disambiguationData":[OSD([subQ0])]});var subQ3=sQuery(id+"F0.wireOp",EDGE,"E10.5");var subQ4=makeQuery(id+"F5.opExtrude","CAP_FACE",FACE,{"disambiguationData":[OSD([subQ0])],"isStart":true});Q0=makeQuery(id+"F5.boolean.opBoolean","SPLIT",EDGE,{"disambiguationData":[topologyDisambiguationEdgeConnected([subQ1,subQ4]),TD([makeQuery(id+"F1.opExtrude","SWEPT_FACE",FACE,{"disambiguationData":[OSD([subQ3])]})])],"derivedFrom":makeQuery(id+"F5.opExtrude","CAP_EDGE",EDGE,{"disambiguationData":[OSD([subQ0])],"isStart":true})});}
            var Q1;
            {var subQ0=sQuery(id+"F4.wireOp",EDGE,"E31");var subQ1=makeQuery(id+"F5.opExtrude","SWEPT_FACE",FACE,{"disambiguationData":[OSD([subQ0])]});var subQ3=sQuery(id+"F0.wireOp",EDGE,"E10.12");var subQ4=makeQuery(id+"F5.opExtrude","CAP_FACE",FACE,{"disambiguationData":[OSD([subQ0])],"isStart":true});Q1=makeQuery(id+"F5.boolean.opBoolean","SPLIT",EDGE,{"disambiguationData":[topologyDisambiguationEdgeConnected([subQ1,subQ4]),TD([makeQuery(id+"F1.opExtrude","SWEPT_FACE",FACE,{"disambiguationData":[OSD([subQ3])]})])],"derivedFrom":makeQuery(id+"F5.opExtrude","CAP_EDGE",EDGE,{"disambiguationData":[OSD([subQ0])],"isStart":true})});}
            var Q2;
            {var subQ0=sQuery(id+"F4.wireOp",EDGE,"E31");var subQ1=makeQuery(id+"F5.opExtrude","SWEPT_FACE",FACE,{"disambiguationData":[OSD([subQ0])]});var subQ2=sQuery(id+"F0.wireOp",EDGE,"E10.1");var subQ4=makeQuery(id+"F5.opExtrude","CAP_FACE",FACE,{"disambiguationData":[OSD([subQ0])],"isStart":true});Q2=makeQuery(id+"F5.boolean.opBoolean","SPLIT",EDGE,{"disambiguationData":[topologyDisambiguationEdgeConnected([subQ1,subQ4]),TD([makeQuery(id+"F1.opExtrude","SWEPT_FACE",FACE,{"disambiguationData":[OSD([subQ2])]})])],"derivedFrom":makeQuery(id+"F5.opExtrude","CAP_EDGE",EDGE,{"disambiguationData":[OSD([subQ0])],"isStart":true})});}
            var Q3;
            {var subQ0=sQuery(id+"F4.wireOp",EDGE,"E31");var subQ1=makeQuery(id+"F5.opExtrude","SWEPT_FACE",FACE,{"disambiguationData":[OSD([subQ0])]});var subQ3=sQuery(id+"F0.wireOp",EDGE,"E10.7");var subQ4=makeQuery(id+"F5.opExtrude","CAP_FACE",FACE,{"disambiguationData":[OSD([subQ0])],"isStart":true});Q3=makeQuery(id+"F5.boolean.opBoolean","SPLIT",EDGE,{"disambiguationData":[topologyDisambiguationEdgeConnected([subQ1,subQ4]),TD([makeQuery(id+"F1.opExtrude","SWEPT_FACE",FACE,{"disambiguationData":[OSD([subQ3])]})])],"derivedFrom":makeQuery(id+"F5.opExtrude","CAP_EDGE",EDGE,{"disambiguationData":[OSD([subQ0])],"isStart":true})});}
            chamfer(context, id + "F10", {"entities" : qUnion([Q0, Q1, Q2, Q3]), "width" : 5 * mm, "tangentPropagation" : true});
        }
        {
            var Q0;
            Q0=makeQuery(id+"F1.opExtrude","CAP_EDGE",EDGE,{"disambiguationData":[OSD([sQuery(id+"F0.wireOp",EDGE,"E10.3")])],"isStart":false});
            var Q1;
            Q1=makeQuery(id+"F1.opExtrude","CAP_EDGE",EDGE,{"disambiguationData":[OSD([sQuery(id+"F0.wireOp",EDGE,"E10.1")])],"isStart":false});
            var Q2;
            Q2=makeQuery(id+"F1.opExtrude","CAP_EDGE",EDGE,{"disambiguationData":[OSD([sQuery(id+"F0.wireOp",EDGE,"E10.14")])],"isStart":false});
            var Q3;
            Q3=makeQuery(id+"F1.opExtrude","CAP_EDGE",EDGE,{"disambiguationData":[OSD([sQuery(id+"F0.wireOp",EDGE,"E10.7")])],"isStart":false});
            var Q4;
            Q4=makeQuery(id+"F1.opExtrude","CAP_EDGE",EDGE,{"disambiguationData":[OSD([sQuery(id+"F0.wireOp",EDGE,"E10.5")])],"isStart":false});
            var Q5;
            Q5=makeQuery(id+"F1.opExtrude","CAP_EDGE",EDGE,{"disambiguationData":[OSD([sQuery(id+"F0.wireOp",EDGE,"E10.10")])],"isStart":false});
            var Q6;
            Q6=makeQuery(id+"F1.opExtrude","CAP_EDGE",EDGE,{"disambiguationData":[OSD([sQuery(id+"F0.wireOp",EDGE,"E10.12")])],"isStart":false});
            var Q7;
            Q7=makeQuery(id+"F1.opExtrude","CAP_EDGE",EDGE,{"disambiguationData":[OSD([sQuery(id+"F0.wireOp",EDGE,"E10.15")])],"isStart":false});
            chamfer(context, id + "F11", {"entities" : qUnion([Q0, Q1, Q2, Q3, Q4, Q5, Q6, Q7]), "width" : 1 * mm, "tangentPropagation" : true});
        }
    });
